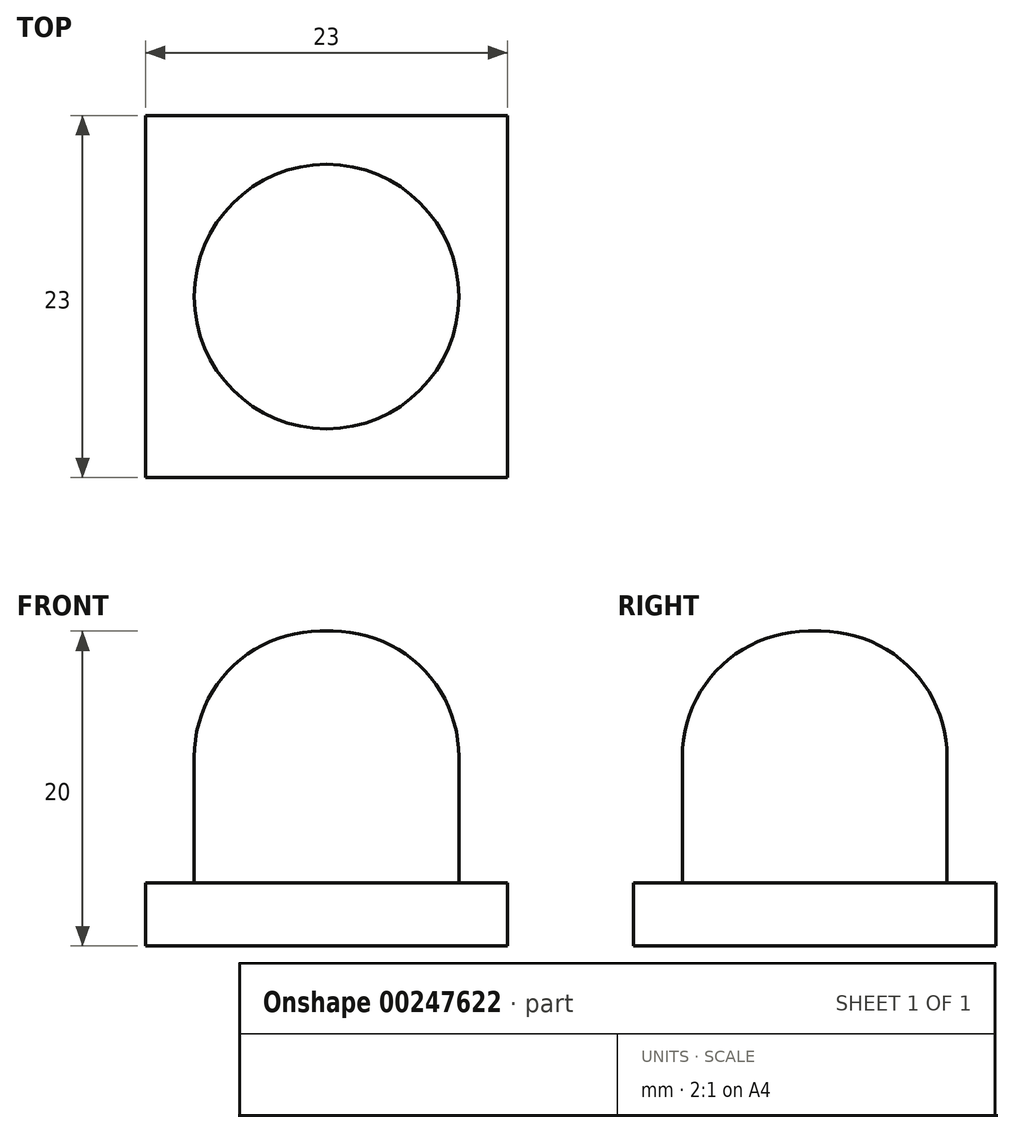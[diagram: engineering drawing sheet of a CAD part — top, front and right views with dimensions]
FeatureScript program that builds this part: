
annotation { "Feature Type Name" : "Feature", "Feature Type Description" : "" }
export const myFeature = defineFeature(function(context is Context, id is Id, definition is map)
    precondition{}
    {
        {
            var Q0;
            Q0=qCreatedBy(makeId("Top.planeOp"),FACE);
            var sketch = newSketch(context, id + "F0", { "sketchPlane" : qUnion([Q0])});
            skLineSegment(sketch, "E0.bottom", {"start": v(-11.5, 11.5) * mm, "end": v(11.5, 11.5) * mm});
            skLineSegment(sketch, "E0.top", {"start": v(-11.5, -11.5) * mm, "end": v(11.5, -11.5) * mm});
            skLineSegment(sketch, "E0.left", {"start": v(-11.5, 11.5) * mm, "end": v(-11.5, -11.5) * mm});
            skLineSegment(sketch, "E0.right", {"start": v(11.5, 11.5) * mm, "end": v(11.5, -11.5) * mm});
            skPoint(sketch, "E0.middle", {"position": v(0, 0) * mm});
            skSolve(sketch);
        }
        {
            var Q0;
            Q0 = qSketchRegion(id + "F0", true);
            extrude(context, id + "F1", {"entities" : qUnion([Q0]), "depth" : 4 * mm});
        }
        {
            var Q0;
            Q0=makeQuery(id+"F1.opExtrude","CAP_FACE",FACE,{"disambiguationData":[OSD([sQuery(id+"F0.wireOp",EDGE,"E0.bottom"),sQuery(id+"F0.wireOp",EDGE,"E0.top"),sQuery(id+"F0.wireOp",EDGE,"E0.left"),sQuery(id+"F0.wireOp",EDGE,"E0.right")])],"isStart":false});
            var sketch = newSketch(context, id + "F2", { "sketchPlane" : qUnion([Q0])});
            skCircle(sketch, "E1", {"center": v(0, 0) * mm, "radius": 8.4 * mm});
            skSolve(sketch);
        }
        {
            var Q0;
            Q0 = qSketchRegion(id + "F2", true);
            extrude(context, id + "F3", {"entities" : qUnion([Q0]), "operationType" : NewBodyOperationType.ADD, "depth" : 16 * mm});
        }
        {
            var Q0;
            Q0=makeQuery(id+"F3.opExtrude","CAP_EDGE",EDGE,{"disambiguationData":[OSD([sQuery(id+"F2.wireOp",EDGE,"E1")])],"isStart":false});
            fillet(context, id + "F4", {"entities" : qUnion([Q0]), "radius" : 8 * mm, "tangentPropagation" : true, "allowEdgeOverflow" : false});
        }
    });
